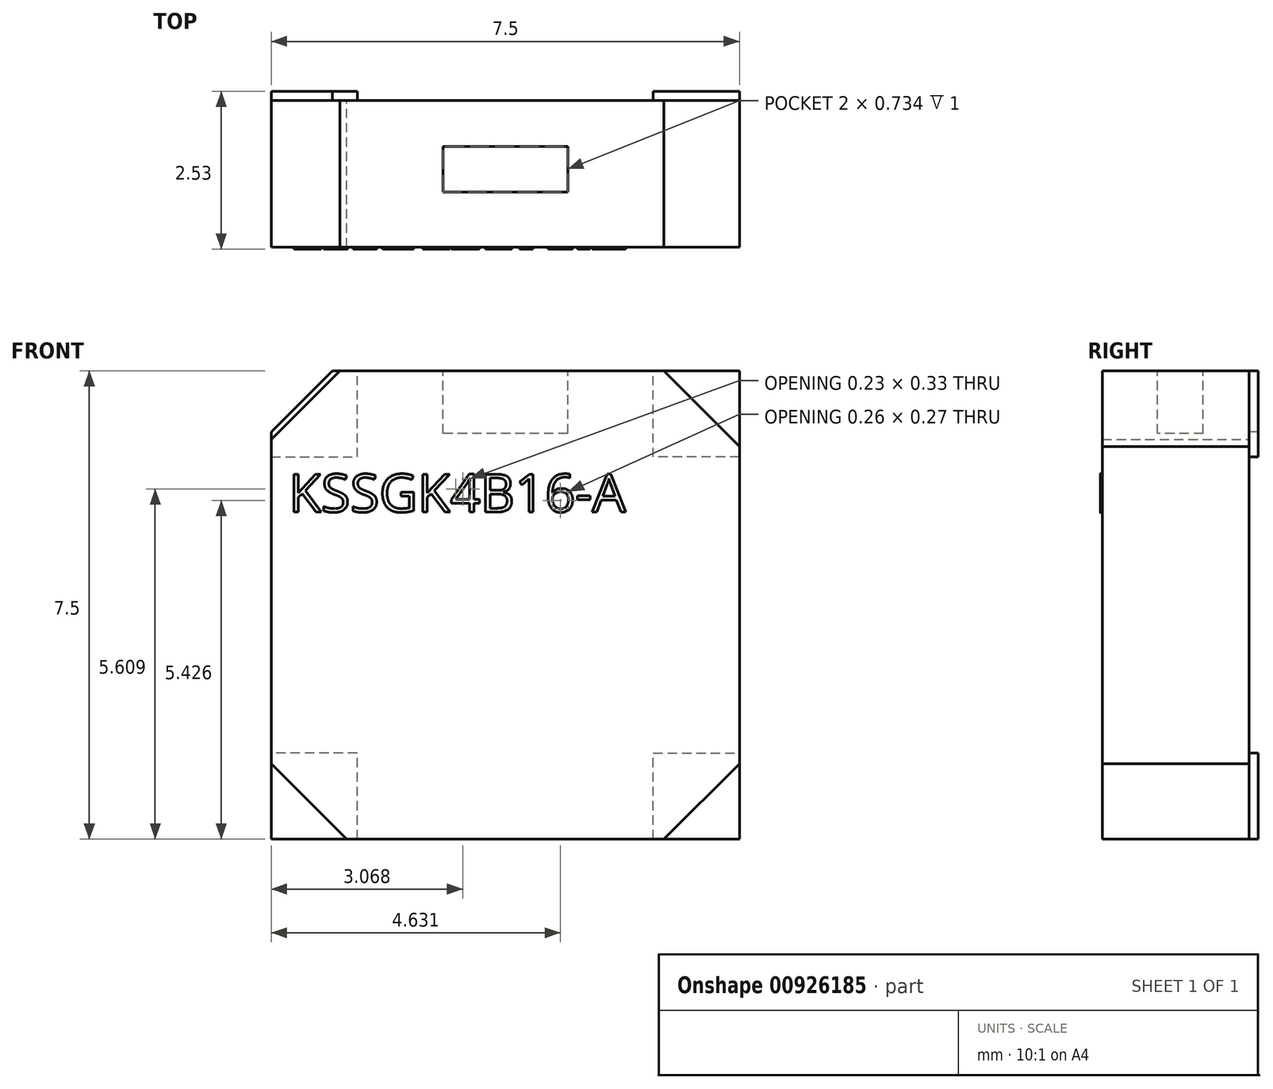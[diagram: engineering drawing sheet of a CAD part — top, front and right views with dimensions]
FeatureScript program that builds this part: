
annotation { "Feature Type Name" : "Feature", "Feature Type Description" : "" }
export const myFeature = defineFeature(function(context is Context, id is Id, definition is map)
    precondition{}
    {
        {
            var Q0;
            Q0=qCreatedBy(makeId("Front.planeOp"),FACE);
            var sketch = newSketch(context, id + "F0", { "sketchPlane" : qUnion([Q0])});
            skLineSegment(sketch, "E0.bottom", {"start": v(-3.75, 3.75) * mm, "end": v(3.75, 3.75) * mm});
            skLineSegment(sketch, "E0.right", {"start": v(3.75, 3.75) * mm, "end": v(3.75, -3.75) * mm});
            skPoint(sketch, "E0.middle", {"position": v(0, 0) * mm});
            skLineSegment(sketch, "E1", {"start": v(-3.75, -2.65) * mm, "end": v(-3.75, 3.75) * mm});
            skLineSegment(sketch, "E2", {"start": v(3.75, -3.75) * mm, "end": v(-2.65, -3.75) * mm});
            skLineSegment(sketch, "E3", {"start": v(-2.65, -3.75) * mm, "end": v(-3.75, -2.65) * mm});
            skSolve(sketch);
        }
        {
            var Q0;
            Q0 = qSketchRegion(id + "F0", true);
            extrude(context, id + "F1", {"entities" : qUnion([Q0]), "depth" : 2.35 * mm, "offsetDistance" : 25 * mm});
        }
        {
            var Q0;
            Q0=makeQuery(id+"F1.opExtrude","SWEPT_EDGE",EDGE,{"disambiguationData":[OSD([sQuery(id+"F0.wireOp",EDGE,"E0.bottom"),sQuery(id+"F0.wireOp",EDGE,"E1")])]});
            chamfer(context, id + "F2", {"entities" : qUnion([Q0]), "width" : 1.21 * mm, "tangentPropagation" : true});
        }
        {
            var Q0;
            Q0=makeQuery(id+"F1.opExtrude","SWEPT_EDGE",EDGE,{"disambiguationData":[OSD([sQuery(id+"F0.wireOp",EDGE,"E0.bottom"),sQuery(id+"F0.wireOp",EDGE,"E0.right")])]});
            chamfer(context, id + "F3", {"entities" : qUnion([Q0]), "width" : 1.21 * mm, "tangentPropagation" : true});
        }
        {
            var Q0;
            Q0=makeQuery(id+"F1.opExtrude","SWEPT_EDGE",EDGE,{"disambiguationData":[OSD([sQuery(id+"F0.wireOp",EDGE,"E0.right"),sQuery(id+"F0.wireOp",EDGE,"E2")])]});
            chamfer(context, id + "F4", {"entities" : qUnion([Q0]), "width" : 1.21 * mm, "tangentPropagation" : true});
        }
        {
            var Q0;
            Q0=makeQuery(id+"F1.opExtrude","SWEPT_FACE",FACE,{"disambiguationData":[OSD([sQuery(id+"F0.wireOp",EDGE,"E1")])]});
            var sketch = newSketch(context, id + "F5", { "sketchPlane" : qUnion([Q0])});
            skLineSegment(sketch, "E4.bottom", {"start": v(0.73, 1) * mm, "end": v(1.47, 1) * mm});
            skLineSegment(sketch, "E4.top", {"start": v(0.73, -1) * mm, "end": v(1.47, -1) * mm});
            skLineSegment(sketch, "E4.left", {"start": v(0.73, 1) * mm, "end": v(0.73, -1) * mm});
            skLineSegment(sketch, "E4.right", {"start": v(1.47, 1) * mm, "end": v(1.47, -1) * mm});
            skSolve(sketch);
        }
        {
            var Q0;
            Q0 = qSketchRegion(id + "F5", true);
            extrude(context, id + "F6", {"entities" : qUnion([Q0]), "operationType" : NewBodyOperationType.REMOVE, "oppositeDirection" : true, "depth" : 1 * mm, "offsetDistance" : 25 * mm});
        }
        {
            var Q0;
            Q0=makeQuery(id+"F1.opExtrude","CAP_FACE",FACE,{"disambiguationData":[OSD([sQuery(id+"F0.wireOp",EDGE,"E0.bottom"),sQuery(id+"F0.wireOp",EDGE,"E0.right"),sQuery(id+"F0.wireOp",EDGE,"E1"),sQuery(id+"F0.wireOp",EDGE,"E2"),sQuery(id+"F0.wireOp",EDGE,"E3")])],"isStart":true});
            var sketch = newSketch(context, id + "F7", { "sketchPlane" : qUnion([Q0])});
            skLineSegment(sketch, "E5.bottom", {"start": v(2.37, 3.75) * mm, "end": v(3.75, 3.75) * mm});
            skLineSegment(sketch, "E5.top", {"start": v(2.37, 2.37) * mm, "end": v(3.75, 2.37) * mm});
            skLineSegment(sketch, "E5.left", {"start": v(2.37, 3.75) * mm, "end": v(2.37, 2.37) * mm});
            skLineSegment(sketch, "E5.right", {"start": v(3.75, 3.75) * mm, "end": v(3.75, 2.37) * mm});
            skLineSegment(sketch, "E6.top", {"start": v(2.37, -2.37) * mm, "end": v(3.75, -2.37) * mm});
            skLineSegment(sketch, "E6.left", {"start": v(2.37, -3.75) * mm, "end": v(2.37, -2.37) * mm});
            skLineSegment(sketch, "E7.bottom", {"start": v(-3.75, -2.37) * mm, "end": v(-2.37, -2.37) * mm});
            skLineSegment(sketch, "E7.top", {"start": v(-3.75, -3.75) * mm, "end": v(-2.37, -3.75) * mm});
            skLineSegment(sketch, "E7.left", {"start": v(-3.75, -2.37) * mm, "end": v(-3.75, -3.75) * mm});
            skLineSegment(sketch, "E7.right", {"start": v(-2.37, -2.37) * mm, "end": v(-2.37, -3.75) * mm});
            skLineSegment(sketch, "E8.bottom", {"start": v(-3.75, 2.37) * mm, "end": v(-2.37, 2.37) * mm});
            skLineSegment(sketch, "E8.top", {"start": v(-3.75, 3.75) * mm, "end": v(-2.37, 3.75) * mm});
            skLineSegment(sketch, "E8.left", {"start": v(-3.75, 2.37) * mm, "end": v(-3.75, 3.75) * mm});
            skLineSegment(sketch, "E8.right", {"start": v(-2.37, 2.37) * mm, "end": v(-2.37, 3.75) * mm});
            skLineSegment(sketch, "E9", {"start": v(2.37, -3.75) * mm, "end": v(2.77, -3.75) * mm});
            skLineSegment(sketch, "E10", {"start": v(3.75, -2.37) * mm, "end": v(3.75, -2.77) * mm});
            skLineSegment(sketch, "E11", {"start": v(2.77, -3.75) * mm, "end": v(3.75, -2.77) * mm});
            skSolve(sketch);
        }
        {
            var Q0;
            Q0 = qSketchRegion(id + "F7", true);
            extrude(context, id + "F8", {"entities" : qUnion([Q0]), "depth" : 0.15 * mm, "offsetDistance" : 25 * mm});
        }
        {
            var Q0;
            Q0=makeQuery(id+"F1.opExtrude","SWEPT_BODY",BODY,{"disambiguationData":[OSD([sQuery(id+"F0.wireOp",EDGE,"E0.bottom"),sQuery(id+"F0.wireOp",EDGE,"E0.right"),sQuery(id+"F0.wireOp",EDGE,"E1"),sQuery(id+"F0.wireOp",EDGE,"E2"),sQuery(id+"F0.wireOp",EDGE,"E3")])]});
            var Q1;
            Q1=makeQuery(id+"F8.opExtrude","SWEPT_BODY",BODY,{"disambiguationData":[OSD([sQuery(id+"F7.wireOp",EDGE,"E5.bottom"),sQuery(id+"F7.wireOp",EDGE,"E5.top"),sQuery(id+"F7.wireOp",EDGE,"E5.left"),sQuery(id+"F7.wireOp",EDGE,"E5.right")])]});
            var Q2;
            Q2=makeQuery(id+"F8.opExtrude","SWEPT_BODY",BODY,{"disambiguationData":[OSD([sQuery(id+"F7.wireOp",EDGE,"E6.top"),sQuery(id+"F7.wireOp",EDGE,"E6.left"),sQuery(id+"F7.wireOp",EDGE,"E9"),sQuery(id+"F7.wireOp",EDGE,"E10"),sQuery(id+"F7.wireOp",EDGE,"E11")])]});
            var Q3;
            Q3=makeQuery(id+"F8.opExtrude","SWEPT_BODY",BODY,{"disambiguationData":[OSD([sQuery(id+"F7.wireOp",EDGE,"E7.bottom"),sQuery(id+"F7.wireOp",EDGE,"E7.top"),sQuery(id+"F7.wireOp",EDGE,"E7.left"),sQuery(id+"F7.wireOp",EDGE,"E7.right")])]});
            var Q4;
            Q4=makeQuery(id+"F8.opExtrude","SWEPT_BODY",BODY,{"disambiguationData":[OSD([sQuery(id+"F7.wireOp",EDGE,"E8.bottom"),sQuery(id+"F7.wireOp",EDGE,"E8.top"),sQuery(id+"F7.wireOp",EDGE,"E8.left"),sQuery(id+"F7.wireOp",EDGE,"E8.right")])]});
            var Q5;
            {var subQ0=sQuery(id+"F0.wireOp",EDGE,"E0.bottom");Q5=makeQuery(id+"F2.opChamfer","BLEND_EDGE",EDGE,{"blendedFrom":[makeQuery(id+"F1.opExtrude","SWEPT_EDGE",EDGE,{"disambiguationData":[OSD([subQ0,sQuery(id+"F0.wireOp",EDGE,"E1")])]}),makeQuery(id+"F1.opExtrude","SWEPT_FACE",FACE,{"disambiguationData":[OSD([subQ0])]})],"blendedInto":[makeQuery(id+"F1.opExtrude","SWEPT_FACE",FACE,{"disambiguationData":[OSD([subQ0])]})]});}
            transform(context, id + "F9", {"entities" : qUnion([Q0, Q1, Q2, Q3, Q4]), "transformType" : TransformType.ROTATION, "transformAxis" : qUnion([Q5]), "angle" : 270 * degree, "makeCopy" : false});
        }
        {
            var Q0;
            Q0=makeQuery(id+"F1.opExtrude","CAP_FACE",FACE,{"disambiguationData":[OSD([sQuery(id+"F0.wireOp",EDGE,"E0.bottom"),sQuery(id+"F0.wireOp",EDGE,"E0.right"),sQuery(id+"F0.wireOp",EDGE,"E1"),sQuery(id+"F0.wireOp",EDGE,"E2"),sQuery(id+"F0.wireOp",EDGE,"E3")])],"isStart":false});
            var sketch = newSketch(context, id + "F10", { "sketchPlane" : qUnion([Q0])});
            skText(sketch, "E12", { "text": "KSSGK4B16-A", "fontName": "OpenSans-Regular.ttf"});
            const initialGuessF10  = {"E12": [-0.00976, 0.0027, 1, 0, 0.00061]};
            skSetInitialGuess(sketch, initialGuessF10);
            skSolve(sketch);
        }
        {
            var Q0;
            Q0 = qSketchRegion(id + "F10", true);
            extrude(context, id + "F11", {"entities" : qUnion([Q0]), "depth" : 0.03 * mm, "offsetDistance" : 25 * mm});
        }
    });
